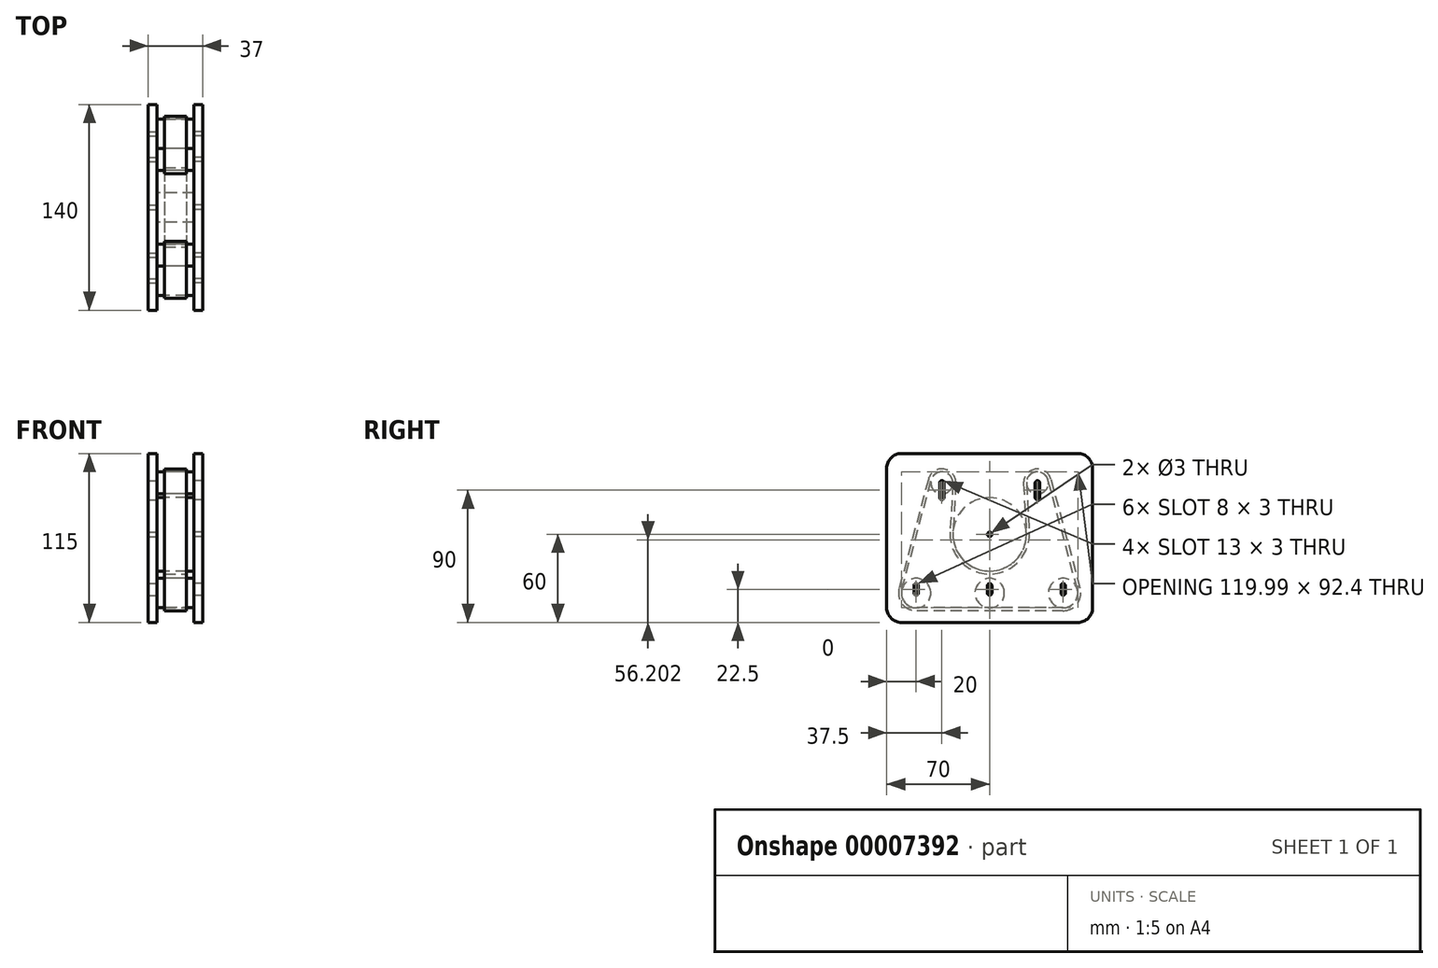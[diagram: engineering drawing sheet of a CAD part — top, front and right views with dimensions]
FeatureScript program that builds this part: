
annotation { "Feature Type Name" : "Feature", "Feature Type Description" : "" }
export const myFeature = defineFeature(function(context is Context, id is Id, definition is map)
    precondition{}
    {
        {
            var Q0;
            Q0=qCreatedBy(makeId("Right.planeOp"),FACE);
            var sketch = newSketch(context, id + "F0", { "sketchPlane" : qUnion([Q0])});
            skCircle(sketch, "E0", {"center": v(0, 0) * mm, "radius": 25 * mm});
            skCircle(sketch, "E1", {"center": v(-50, -40) * mm, "radius": 10 * mm});
            skCircle(sketch, "E2", {"center": v(0, -40) * mm, "radius": 10 * mm});
            skCircle(sketch, "E3", {"center": v(50, -40) * mm, "radius": 10 * mm});
            skLineSegment(sketch, "E4", {"start": v(0, -40) * mm, "end": v(0, 0) * mm});
            skLineSegment(sketch, "E5", {"start": v(0, -40) * mm, "end": v(50, -40) * mm});
            skLineSegment(sketch, "E6", {"start": v(0, -40) * mm, "end": v(-50, -40) * mm});
            skCircle(sketch, "E7", {"center": v(-32.5, 35) * mm, "radius": 7.5 * mm});
            skCircle(sketch, "E8", {"center": v(32.5, 35) * mm, "radius": 7.5 * mm});
            skLineSegment(sketch, "E9", {"start": v(-32.5, 35) * mm, "end": v(32.5, 35) * mm});
            skLineSegment(sketch, "E10", {"start": v(-25, 35) * mm, "end": v(-25, 0) * mm, "construction": true});
            skLineSegment(sketch, "E11", {"start": v(25, 35) * mm, "end": v(25, 0) * mm, "construction": true});
            skSolve(sketch);
        }
        {
            var Q0;
            {var subQ0=sQuery(id+"F0.wireOp",EDGE,"E0");var subQ3=makeQuery(id+"F0.imprint","INTERSECT",VERTEX,{"derivedFrom":[subQ0,sQuery(id+"F0.wireOp",EDGE,"51fb4b48-1cf9-4805-a192-ab41fcaa3eb0")]});Q0=makeQuery(id+"F0.imprint","IMPRINT",FACE,{"disambiguationData":[TD([[makeQuery(id+"F0.imprint","IMPRINT",EDGE,{"disambiguationData":[TD([[subQ3,1.0]])],"derivedFrom":subQ0}),1.0]])]});}
            var Q1;
            Q1=makeQuery(id+"F0.imprint","IMPRINT",FACE,{"disambiguationData":[TD([[makeQuery(id+"F0.imprint","IMPRINT",EDGE,{"derivedFrom":sQuery(id+"F0.wireOp",EDGE,"E7")}),1.0]])]});
            var Q2;
            Q2=makeQuery(id+"F0.imprint","IMPRINT",FACE,{"disambiguationData":[TD([[makeQuery(id+"F0.imprint","IMPRINT",EDGE,{"derivedFrom":sQuery(id+"F0.wireOp",EDGE,"E8")}),1.0]])]});
            var Q3;
            Q3=makeQuery(id+"F0.imprint","IMPRINT",FACE,{"disambiguationData":[TD([[makeQuery(id+"F0.imprint","IMPRINT",EDGE,{"derivedFrom":sQuery(id+"F0.wireOp",EDGE,"E3")}),1.0]])]});
            var Q4;
            {var subQ0=sQuery(id+"F0.wireOp",EDGE,"E5");var subQ1=sQuery(id+"F0.wireOp",EDGE,"E2");var subQ2=makeQuery(id+"F0.imprint","INTERSECT",VERTEX,{"derivedFrom":[subQ1,subQ0]});Q4=makeQuery(id+"F0.imprint","IMPRINT",FACE,{"disambiguationData":[TD([[makeQuery(id+"F0.imprint","IMPRINT",EDGE,{"disambiguationData":[TD([[subQ2,-1.0]])],"derivedFrom":subQ1}),1.0]])]});}
            var Q5;
            {var subQ1=sQuery(id+"F0.wireOp",EDGE,"E2");var subQ3=sQuery(id+"F0.wireOp",EDGE,"E5");var subQ5=makeQuery(id+"F0.imprint","INTERSECT",VERTEX,{"derivedFrom":[subQ1,subQ3]});Q5=makeQuery(id+"F0.imprint","IMPRINT",FACE,{"disambiguationData":[TD([[makeQuery(id+"F0.imprint","IMPRINT",EDGE,{"disambiguationData":[TD([[subQ5,1.0]])],"derivedFrom":subQ1}),1.0]])]});}
            var Q6;
            {var subQ0=sQuery(id+"F0.wireOp",EDGE,"E6");var subQ1=sQuery(id+"F0.wireOp",EDGE,"E2");var subQ2=makeQuery(id+"F0.imprint","INTERSECT",VERTEX,{"derivedFrom":[subQ1,subQ0]});Q6=makeQuery(id+"F0.imprint","IMPRINT",FACE,{"disambiguationData":[TD([[makeQuery(id+"F0.imprint","IMPRINT",EDGE,{"disambiguationData":[TD([[subQ2,1.0]])],"derivedFrom":subQ1}),1.0]])]});}
            var Q7;
            Q7=makeQuery(id+"F0.imprint","IMPRINT",FACE,{"disambiguationData":[TD([[makeQuery(id+"F0.imprint","IMPRINT",EDGE,{"derivedFrom":sQuery(id+"F0.wireOp",EDGE,"E1")}),1.0]])]});
            var Q8;
            Q8=makeQuery(id+"F0.imprint","IMPRINT",FACE,{"disambiguationData":[TD([[makeQuery(id+"F0.imprint","IMPRINT",EDGE,{"derivedFrom":sQuery(id+"F0.wireOp",EDGE,"E0")}),1.0]])]});
            extrude(context, id + "F1", {"entities" : qUnion([Q0, Q1, Q2, Q3, Q4, Q5, Q6, Q7, Q8]), "depth" : 25 * mm});
        }
        {
            var Q0;
            Q0=makeQuery(id+"F1.opExtrude","CAP_FACE",FACE,{"disambiguationData":[OSD([sQuery(id+"F0.wireOp",EDGE,"E0")])],"isStart":false});
            var sketch = newSketch(context, id + "F2", { "sketchPlane" : qUnion([Q0])});
            skArc(sketch, "E12.0", {"start": v(-25, 35) * mm, "mid": v(-31.52, 42.44) * mm, "end": v(-39.74, 36.94) * mm});
            skArc(sketch, "E12.1", {"start": v(39.74, 36.94) * mm, "mid": v(31.52, 42.44) * mm, "end": v(25, 35) * mm});
            skArc(sketch, "E12.2", {"start": v(-25, 0) * mm, "mid": v(0, -25) * mm, "end": v(25, 0) * mm});
            skArc(sketch, "E12.3", {"start": v(50, -50) * mm, "mid": v(57.93, -46.09) * mm, "end": v(59.66, -37.41) * mm});
            skArc(sketch, "E12.5", {"start": v(-59.66, -37.41) * mm, "mid": v(-57.93, -46.09) * mm, "end": v(-50, -50) * mm});
            skLineSegment(sketch, "E13", {"start": v(-39.74, 36.94) * mm, "end": v(-59.66, -37.41) * mm});
            skLineSegment(sketch, "E14", {"start": v(-50, -50) * mm, "end": v(50, -50) * mm});
            skLineSegment(sketch, "E15", {"start": v(39.74, 36.94) * mm, "end": v(59.66, -37.41) * mm});
            skLineSegment(sketch, "E16", {"start": v(-25, 35) * mm, "end": v(-25, 0) * mm});
            skLineSegment(sketch, "E17", {"start": v(25, 35) * mm, "end": v(25, 0) * mm});
            skSolve(sketch);
        }
        {
            var Q0;
            Q0=sQuery(id+"F2.wireOp",EDGE,"E13");
            var Q1;
            Q1=sQuery(id+"F2.wireOp",EDGE,"E12.0");
            var Q2;
            Q2=sQuery(id+"F2.wireOp",EDGE,"E16");
            var Q3;
            Q3=sQuery(id+"F2.wireOp",EDGE,"E12.2");
            var Q4;
            Q4=sQuery(id+"F2.wireOp",EDGE,"E17");
            var Q5;
            Q5=sQuery(id+"F2.wireOp",EDGE,"E12.1");
            var Q6;
            Q6=sQuery(id+"F2.wireOp",EDGE,"E15");
            var Q7;
            Q7=sQuery(id+"F2.wireOp",EDGE,"E12.3");
            var Q8;
            Q8=sQuery(id+"F2.wireOp",EDGE,"E14");
            var Q9;
            Q9=sQuery(id+"F2.wireOp",EDGE,"E12.5");
            extrude(context, id + "F3", {"bodyType" : ToolBodyType.SURFACE, "surfaceEntities" : qUnion([Q0, Q1, Q2, Q3, Q4, Q5, Q6, Q7, Q8, Q9]), "oppositeDirection" : true, "depth" : 25 * mm});
        }
        {
            var Q0;
            Q0=makeQuery(id+"F1.opExtrude","CAP_FACE",FACE,{"disambiguationData":[OSD([sQuery(id+"F0.wireOp",EDGE,"E0")])],"isStart":false});
            var sketch = newSketch(context, id + "F4", { "sketchPlane" : qUnion([Q0])});
            skCircle(sketch, "E18.0", {"center": v(-32.5, 35) * mm, "radius": 7.5 * mm, "construction": true});
            skCircle(sketch, "E18.1", {"center": v(0, 0) * mm, "radius": 25 * mm, "construction": true});
            skCircle(sketch, "E18.2", {"center": v(32.5, 35) * mm, "radius": 7.5 * mm, "construction": true});
            skCircle(sketch, "E18.3", {"center": v(50, -40) * mm, "radius": 10 * mm, "construction": true});
            skCircle(sketch, "E18.4", {"center": v(0, -40) * mm, "radius": 10 * mm, "construction": true});
            skCircle(sketch, "E18.5", {"center": v(-50, -40) * mm, "radius": 10 * mm, "construction": true});
            skCircle(sketch, "E19", {"center": v(0, 0) * mm, "radius": 1.5 * mm});
            skLineSegment(sketch, "E20", {"start": v(0, -40) * mm, "end": v(0, 0) * mm, "construction": true});
            skCircle(sketch, "E21", {"center": v(-50, -40) * mm, "radius": 1.5 * mm});
            skLineSegment(sketch, "E22", {"start": v(-50, -40) * mm, "end": v(-50, -35) * mm});
            skCircle(sketch, "E23", {"center": v(-50, -35) * mm, "radius": 1.5 * mm});
            skLineSegment(sketch, "E24", {"start": v(-51.5, -35) * mm, "end": v(-51.5, -40) * mm});
            skLineSegment(sketch, "E25", {"start": v(-48.5, -35) * mm, "end": v(-48.5, -40) * mm});
            skLineSegment(sketch, "E26.0.MirrorCS", {"start": v(50, -40) * mm, "end": v(50, -35) * mm});
            skLineSegment(sketch, "E26.1.MirrorCS", {"start": v(48.5, -35) * mm, "end": v(48.5, -40) * mm});
            skLineSegment(sketch, "E26.2.MirrorCS", {"start": v(51.5, -35) * mm, "end": v(51.5, -40) * mm});
            skCircle(sketch, "E26.3.MirrorC", {"center": v(50, -40) * mm, "radius": 1.5 * mm});
            skCircle(sketch, "E26.4.MirrorC", {"center": v(50, -35) * mm, "radius": 1.5 * mm});
            skCircle(sketch, "E27.1.0.0", {"center": v(0, -40) * mm, "radius": 1.5 * mm});
            skLineSegment(sketch, "E27.1.0.1", {"start": v(-1.5, -35) * mm, "end": v(-1.5, -40) * mm});
            skLineSegment(sketch, "E27.1.0.2", {"start": v(1.5, -35) * mm, "end": v(1.5, -40) * mm});
            skCircle(sketch, "E27.1.0.3", {"center": v(0, -35) * mm, "radius": 1.5 * mm});
            skLineSegment(sketch, "E27.1.0.4", {"start": v(0, -40) * mm, "end": v(0, -35) * mm});
            skLineSegment(sketch, "E27.direction1", {"start": v(-50, -40) * mm, "end": v(0, -40) * mm, "construction": true});
            skCircle(sketch, "E28", {"center": v(-32.5, 35) * mm, "radius": 1.5 * mm});
            skCircle(sketch, "E29", {"center": v(-32.5, 25) * mm, "radius": 1.5 * mm});
            skLineSegment(sketch, "E30", {"start": v(-32.5, 35) * mm, "end": v(-32.5, 25) * mm, "construction": true});
            skLineSegment(sketch, "E31", {"start": v(-34, 35) * mm, "end": v(-34, 25) * mm});
            skLineSegment(sketch, "E32", {"start": v(-31, 35) * mm, "end": v(-31, 25) * mm});
            skLineSegment(sketch, "E33.0.MirrorCS", {"start": v(32.5, 35) * mm, "end": v(32.5, 25) * mm, "construction": true});
            skLineSegment(sketch, "E33.1.MirrorCS", {"start": v(31, 35) * mm, "end": v(31, 25) * mm});
            skLineSegment(sketch, "E33.2.MirrorCS", {"start": v(34, 35) * mm, "end": v(34, 25) * mm});
            skCircle(sketch, "E33.3.MirrorC", {"center": v(32.5, 25) * mm, "radius": 1.5 * mm});
            skCircle(sketch, "E33.4.MirrorC", {"center": v(32.5, 35) * mm, "radius": 1.5 * mm});
            skLineSegment(sketch, "E34.rect.bottom", {"start": v(60, 55) * mm, "end": v(-60, 55) * mm});
            skLineSegment(sketch, "E34.rect.top", {"start": v(60, -60) * mm, "end": v(-60, -60) * mm});
            skLineSegment(sketch, "E34.rect.left", {"start": v(70, 45) * mm, "end": v(70, -50) * mm});
            skLineSegment(sketch, "E34.rect.right", {"start": v(-70, 45) * mm, "end": v(-70, -50) * mm});
            skPoint(sketch, "E34.rect.middle", {"position": v(0, -2.5) * mm});
            skPoint(sketch, "E35.visualSharp", {"position": v(-70, 55) * mm});
            skArc(sketch, "E35.filletArc", {"start": v(-60, 55) * mm, "mid": v(-67.07, 52.07) * mm, "end": v(-70, 45) * mm});
            skPoint(sketch, "E36.visualSharp", {"position": v(-70, -60) * mm});
            skArc(sketch, "E36.filletArc", {"start": v(-70, -50) * mm, "mid": v(-67.07, -57.07) * mm, "end": v(-60, -60) * mm});
            skPoint(sketch, "E37.visualSharp", {"position": v(70, -60) * mm});
            skArc(sketch, "E37.filletArc", {"start": v(60, -60) * mm, "mid": v(67.07, -57.07) * mm, "end": v(70, -50) * mm});
            skPoint(sketch, "E38.visualSharp", {"position": v(70, 55) * mm});
            skArc(sketch, "E38.filletArc", {"start": v(70, 45) * mm, "mid": v(67.07, 52.07) * mm, "end": v(60, 55) * mm});
            skSolve(sketch);
        }
        {
            var Q0;
            {var subQ2=sQuery(id+"F4.wireOp",EDGE,"E24");Q0=makeQuery(id+"F4.imprint","IMPRINT",FACE,{"disambiguationData":[TD([[makeQuery(id+"F4.imprint","IMPRINT",EDGE,{"derivedFrom":subQ2}),-1.0]])]});}
            var Q1;
            Q1=makeQuery(id+"F4.imprint","IMPRINT",FACE,{"disambiguationData":[TD([[makeQuery(id+"F4.imprint","IMPRINT",EDGE,{"derivedFrom":sQuery(id+"F4.wireOp",EDGE,"E19")}),-1.0]])]});
            extrude(context, id + "F5", {"entities" : qUnion([Q0, Q1]), "depth" : 6 * mm});
        }
        {
            var Q0;
            Q0=makeQuery(id+"F5.opExtrude","CAP_FACE",FACE,{"disambiguationData":[OSD([sQuery(id+"F4.wireOp",EDGE,"E19"),sQuery(id+"F4.wireOp",EDGE,"E21"),sQuery(id+"F4.wireOp",EDGE,"E23"),sQuery(id+"F4.wireOp",EDGE,"E24"),sQuery(id+"F4.wireOp",EDGE,"E25"),sQuery(id+"F4.wireOp",EDGE,"E26.1.MirrorCS"),sQuery(id+"F4.wireOp",EDGE,"E26.2.MirrorCS"),sQuery(id+"F4.wireOp",EDGE,"E26.3.MirrorC"),sQuery(id+"F4.wireOp",EDGE,"E26.4.MirrorC"),sQuery(id+"F4.wireOp",EDGE,"E27.1.0.0"),sQuery(id+"F4.wireOp",EDGE,"E27.1.0.1"),sQuery(id+"F4.wireOp",EDGE,"E27.1.0.2"),sQuery(id+"F4.wireOp",EDGE,"E27.1.0.3"),sQuery(id+"F4.wireOp",EDGE,"E28"),sQuery(id+"F4.wireOp",EDGE,"E29"),sQuery(id+"F4.wireOp",EDGE,"E31"),sQuery(id+"F4.wireOp",EDGE,"E32"),sQuery(id+"F4.wireOp",EDGE,"E33.1.MirrorCS"),sQuery(id+"F4.wireOp",EDGE,"E33.2.MirrorCS"),sQuery(id+"F4.wireOp",EDGE,"E33.3.MirrorC"),sQuery(id+"F4.wireOp",EDGE,"E33.4.MirrorC"),sQuery(id+"F4.wireOp",EDGE,"E34.rect.bottom"),sQuery(id+"F4.wireOp",EDGE,"E34.rect.top"),sQuery(id+"F4.wireOp",EDGE,"E34.rect.left"),sQuery(id+"F4.wireOp",EDGE,"E34.rect.right"),sQuery(id+"F4.wireOp",EDGE,"E35.filletArc"),sQuery(id+"F4.wireOp",EDGE,"E36.filletArc"),sQuery(id+"F4.wireOp",EDGE,"E37.filletArc"),sQuery(id+"F4.wireOp",EDGE,"E38.filletArc")])],"isStart":true});
            cPlane(context, id + "F6", {"entities" : qUnion([Q0]), "cplaneType" : CPlaneType.OFFSET, "offset" : 5 * mm, "width" : 150 * mm, "height" : 150 * mm});
        }
        {
            var Q0;
            Q0=qCreatedBy(id+"F6.planeOp",FACE);
            var sketch = newSketch(context, id + "F7", { "sketchPlane" : qUnion([Q0])});
            skCircle(sketch, "E39.0", {"center": v(-32.5, 35) * mm, "radius": 7.5 * mm});
            skCircle(sketch, "E39.1", {"center": v(-50, -40) * mm, "radius": 10 * mm});
            skCircle(sketch, "E39.2", {"center": v(0, -40) * mm, "radius": 10 * mm, "construction": true});
            skCircle(sketch, "E39.3", {"center": v(50, -40) * mm, "radius": 10 * mm});
            skCircle(sketch, "E39.4", {"center": v(32.5, 35) * mm, "radius": 7.5 * mm});
            skLineSegment(sketch, "E40", {"start": v(-59.66, -37.41) * mm, "end": v(-57.94, -31) * mm});
            skLineSegment(sketch, "E41", {"start": v(-50, -50) * mm, "end": v(50, -50) * mm});
            skLineSegment(sketch, "E42", {"start": v(59.66, -37.41) * mm, "end": v(57.94, -31) * mm});
            skLineSegment(sketch, "E43", {"start": v(-23.02, 34.44) * mm, "end": v(-23.02, 34.44) * mm});
            skLineSegment(sketch, "E44", {"start": v(23.02, 34.44) * mm, "end": v(24.36, 11.65) * mm});
            skLineSegment(sketch, "E45", {"start": v(-25.01, 34.56) * mm, "end": v(-26.95, 1.59) * mm});
            skLineSegment(sketch, "E46", {"start": v(25.01, 34.56) * mm, "end": v(26.95, 1.59) * mm});
            skLineSegment(sketch, "E47", {"start": v(-41.68, 37.46) * mm, "end": v(-61.6, -36.9) * mm});
            skLineSegment(sketch, "E48", {"start": v(-50, -52) * mm, "end": v(50, -52) * mm});
            skLineSegment(sketch, "E49", {"start": v(41.68, 37.46) * mm, "end": v(61.6, -36.9) * mm});
            skArc(sketch, "E50", {"start": v(-41.25, 31.3) * mm, "mid": v(-23.75, 38.7) * mm, "end": v(-41.25, 31.3) * mm});
            skArc(sketch, "E51", {"start": v(-25.36, 28.74) * mm, "mid": v(-39.64, 41.26) * mm, "end": v(-25.36, 28.74) * mm});
            skArc(sketch, "E52", {"start": v(-41.68, 37.46) * mm, "mid": v(-41.98, 34.35) * mm, "end": v(-41.25, 31.3) * mm, "construction": true});
            skArc(sketch, "E53", {"start": v(-41.25, 31.3) * mm, "mid": v(-34.02, 25.62) * mm, "end": v(-25.36, 28.74) * mm, "construction": true});
            skLineSegment(sketch, "E54", {"start": v(-23.02, 34.44) * mm, "end": v(-24.36, 11.65) * mm});
            skArc(sketch, "E55", {"start": v(-25.36, 28.74) * mm, "mid": v(-23.71, 31.4) * mm, "end": v(-23.02, 34.44) * mm, "construction": true});
            skArc(sketch, "E56", {"start": v(-23.02, 34.44) * mm, "mid": v(-30.98, 44.38) * mm, "end": v(-41.68, 37.46) * mm});
            skArc(sketch, "E57", {"start": v(-25.36, 28.74) * mm, "mid": v(-39.64, 41.26) * mm, "end": v(-25.36, 28.74) * mm, "construction": true});
            skLineSegment(sketch, "E58", {"start": v(-24.36, 11.65) * mm, "end": v(-24.96, 1.47) * mm});
            skLineSegment(sketch, "E59", {"start": v(-24.36, 11.65) * mm, "end": v(-24.36, 11.65) * mm});
            skLineSegment(sketch, "E60", {"start": v(-26.95, 1.59) * mm, "end": v(-26.95, 1.59) * mm});
            skArc(sketch, "E61", {"start": v(-24.36, 11.65) * mm, "mid": v(-26.14, 6.74) * mm, "end": v(-26.95, 1.59) * mm, "construction": true});
            skArc(sketch, "E62", {"start": v(-26.95, 1.59) * mm, "mid": v(0, -27) * mm, "end": v(26.95, 1.59) * mm});
            skLineSegment(sketch, "E63", {"start": v(24.36, 11.65) * mm, "end": v(24.96, 1.47) * mm});
            skArc(sketch, "E64", {"start": v(26.95, 1.59) * mm, "mid": v(26.14, 6.74) * mm, "end": v(24.36, 11.65) * mm, "construction": true});
            skArc(sketch, "E65", {"start": v(24.36, 11.65) * mm, "mid": v(0, 27) * mm, "end": v(-24.36, 11.65) * mm, "construction": true});
            skArc(sketch, "E66", {"start": v(23.02, 34.44) * mm, "mid": v(23.71, 31.4) * mm, "end": v(25.36, 28.74) * mm, "construction": true});
            skArc(sketch, "E67", {"start": v(25.36, 28.74) * mm, "mid": v(34.02, 25.62) * mm, "end": v(41.25, 31.3) * mm, "construction": true});
            skArc(sketch, "E68", {"start": v(41.25, 31.3) * mm, "mid": v(41.98, 34.35) * mm, "end": v(41.68, 37.46) * mm, "construction": true});
            skArc(sketch, "E69", {"start": v(41.68, 37.46) * mm, "mid": v(30.98, 44.38) * mm, "end": v(23.02, 34.44) * mm});
            skLineSegment(sketch, "E70", {"start": v(57.94, -31) * mm, "end": v(39.74, 36.94) * mm});
            skArc(sketch, "E71", {"start": v(61.6, -36.9) * mm, "mid": v(60.2, -33.68) * mm, "end": v(57.94, -31) * mm, "construction": true});
            skArc(sketch, "E72", {"start": v(57.94, -31) * mm, "mid": v(40.48, -32.7) * mm, "end": v(43.37, -50) * mm, "construction": true});
            skArc(sketch, "E73", {"start": v(50, -52) * mm, "mid": v(59.52, -47.3) * mm, "end": v(61.6, -36.9) * mm});
            skArc(sketch, "E74", {"start": v(43.37, -50) * mm, "mid": v(46.54, -51.49) * mm, "end": v(50, -52) * mm, "construction": true});
            skLineSegment(sketch, "E75", {"start": v(-57.94, -31) * mm, "end": v(-39.74, 36.94) * mm});
            skArc(sketch, "E76", {"start": v(-61.6, -36.9) * mm, "mid": v(-59.52, -47.3) * mm, "end": v(-50, -52) * mm});
            skArc(sketch, "E77", {"start": v(-57.94, -31) * mm, "mid": v(-60.2, -33.68) * mm, "end": v(-61.6, -36.9) * mm, "construction": true});
            skArc(sketch, "E78", {"start": v(-43.37, -50) * mm, "mid": v(-40.48, -32.7) * mm, "end": v(-57.94, -31) * mm, "construction": true});
            skArc(sketch, "E79", {"start": v(-50, -52) * mm, "mid": v(-46.54, -51.49) * mm, "end": v(-43.37, -50) * mm, "construction": true});
            skArc(sketch, "E80", {"start": v(-24.96, 1.47) * mm, "mid": v(0, -25) * mm, "end": v(24.96, 1.47) * mm});
            skArc(sketch, "E81", {"start": v(24.96, 1.47) * mm, "mid": v(0, 25) * mm, "end": v(-24.96, 1.47) * mm, "construction": true});
            skSolve(sketch);
        }
        {
            var Q0;
            Q0 = qSketchRegion(id + "F7", true);
            extrude(context, id + "F8", {"entities" : qUnion([Q0]), "depth" : 15 * mm});
        }
        {
            var Q0;
            Q0=makeQuery(id+"F1.opExtrude","CAP_FACE",FACE,{"disambiguationData":[OSD([sQuery(id+"F0.wireOp",EDGE,"E0")])],"isStart":true});
            var Q1;
            Q1=makeQuery(id+"F1.opExtrude","CAP_FACE",FACE,{"disambiguationData":[OSD([sQuery(id+"F0.wireOp",EDGE,"E8")])],"isStart":false});
            cPlane(context, id + "F9", {"entities" : qUnion([Q0, Q1]), "cplaneType" : CPlaneType.MID_PLANE, "offset" : 150 * mm, "width" : 150 * mm, "height" : 150 * mm});
        }
        {
            var Q0;
            Q0=makeQuery(id+"F5.opExtrude","SWEPT_BODY",BODY,{"disambiguationData":[OSD([sQuery(id+"F4.wireOp",EDGE,"E19"),sQuery(id+"F4.wireOp",EDGE,"E21"),sQuery(id+"F4.wireOp",EDGE,"E23"),sQuery(id+"F4.wireOp",EDGE,"E24"),sQuery(id+"F4.wireOp",EDGE,"E25"),sQuery(id+"F4.wireOp",EDGE,"E26.1.MirrorCS"),sQuery(id+"F4.wireOp",EDGE,"E26.2.MirrorCS"),sQuery(id+"F4.wireOp",EDGE,"E26.3.MirrorC"),sQuery(id+"F4.wireOp",EDGE,"E26.4.MirrorC"),sQuery(id+"F4.wireOp",EDGE,"E27.1.0.0"),sQuery(id+"F4.wireOp",EDGE,"E27.1.0.1"),sQuery(id+"F4.wireOp",EDGE,"E27.1.0.2"),sQuery(id+"F4.wireOp",EDGE,"E27.1.0.3"),sQuery(id+"F4.wireOp",EDGE,"E28"),sQuery(id+"F4.wireOp",EDGE,"E29"),sQuery(id+"F4.wireOp",EDGE,"E31"),sQuery(id+"F4.wireOp",EDGE,"E32"),sQuery(id+"F4.wireOp",EDGE,"E33.1.MirrorCS"),sQuery(id+"F4.wireOp",EDGE,"E33.2.MirrorCS"),sQuery(id+"F4.wireOp",EDGE,"E33.3.MirrorC"),sQuery(id+"F4.wireOp",EDGE,"E33.4.MirrorC"),sQuery(id+"F4.wireOp",EDGE,"E34.rect.bottom"),sQuery(id+"F4.wireOp",EDGE,"E34.rect.top"),sQuery(id+"F4.wireOp",EDGE,"E34.rect.left"),sQuery(id+"F4.wireOp",EDGE,"E34.rect.right"),sQuery(id+"F4.wireOp",EDGE,"E35.filletArc"),sQuery(id+"F4.wireOp",EDGE,"E36.filletArc"),sQuery(id+"F4.wireOp",EDGE,"E37.filletArc"),sQuery(id+"F4.wireOp",EDGE,"E38.filletArc")])]});
            var Q1;
            Q1=qCreatedBy(id+"F9.planeOp",FACE);
            mirror(context, id + "F10", {"entities" : qUnion([Q0]), "mirrorPlane" : qUnion([Q1])});
        }
    });
